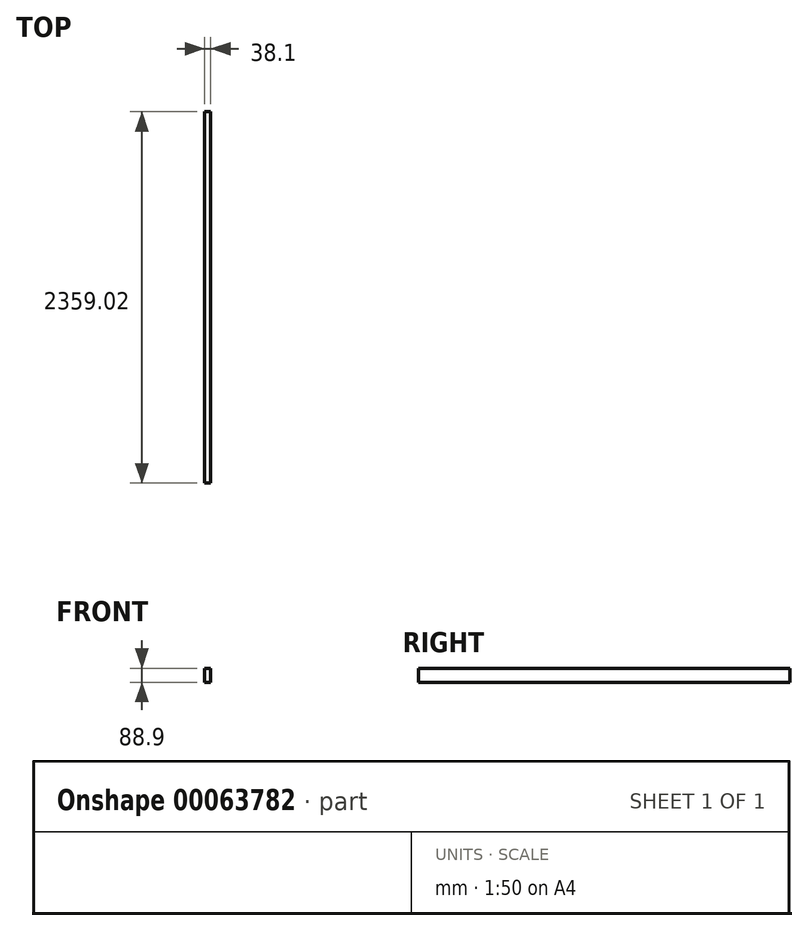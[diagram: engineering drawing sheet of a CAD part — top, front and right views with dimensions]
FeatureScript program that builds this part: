
annotation { "Feature Type Name" : "Feature", "Feature Type Description" : "" }
export const myFeature = defineFeature(function(context is Context, id is Id, definition is map)
    precondition{}
    {
        {
            var Q0;
            Q0=qCreatedBy(makeId("Front.planeOp"),FACE);
            var sketch = newSketch(context, id + "F0", { "sketchPlane" : qUnion([Q0])});
            skLineSegment(sketch, "E0.bottom", {"start": v(-18, 55.77) * mm, "end": v(20.1, 55.77) * mm});
            skLineSegment(sketch, "E0.top", {"start": v(-18, -33.13) * mm, "end": v(20.1, -33.13) * mm});
            skLineSegment(sketch, "E0.left", {"start": v(-18, 55.77) * mm, "end": v(-18, -33.13) * mm});
            skLineSegment(sketch, "E0.right", {"start": v(20.1, 55.77) * mm, "end": v(20.1, -33.13) * mm});
            skSolve(sketch);
        }
        {
            var Q0;
            Q0 = qSketchRegion(id + "F0", true);
            extrude(context, id + "F1", {"entities" : qUnion([Q0]), "endBound" : BoundingType.SYMMETRIC, "depth" : 2359.03 * mm});
        }
    });
